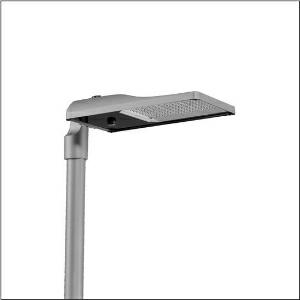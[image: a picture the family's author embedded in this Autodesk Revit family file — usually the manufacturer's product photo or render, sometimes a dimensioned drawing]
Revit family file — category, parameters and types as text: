
# Revit family: streetlight_sl_31_maxi___st0_5a_5xh8b31t08sa_315f
name_source: partatom
category: Lighting Fixtures
units: mm (PartAtom-declared; Revit-internal decimal feet)

## family parameters
Cut with Voids When Loaded = No
Host = Face
Light Source = No
Part Type = Normal
Room Calculation Point = No
Round Connector Dimension = Use Diameter
Shared = No

## types (1)
- --- (1 x LED, 28310 lm, 211.4 W, 3000K)
    Apparent Load = 211 VA
    CIE Flux Codes = 41 75 97 100 100
    Color Rendering = 70
    Color Temperature = 3000K
    Default Elevation = 1800 mm
    Description = Streetlight SL 31 maxi D4i, Desk-Remote mast luminaire for post-top, side-entry; light control with lens of PMMA; light distribution: ST0.5a, direct asymmetric distribution, for standard-compliant lighting for roads and squares; LED: luminous flux: 28.310lm, light colour: 730, colour temperature: 3000K; luminous efficacy: 133,9lm/W; control: pre-setting: logarithmic dimming characteristic, flexible luminous flux parameterisation, time-dependent luminous flux control, constant luminous flux control, power reduction, intelligent temperature release in ECG and LED module, overheat protection; luminaire housing, of diecast aluminium, SITECO metallic grey (DB 702S), corrosivity category C5 high according to DIN EN ISO 12944; cover of toughened safety glass, transparent, opened without tools; mast flange of diecast aluminium, SITECO metallic grey (DB 702S), spigot size: 76/60mm, mast flange included unmounted; cable length: 14,5m, connection cable pre-assembled; mains connection: 220..240V, AC, 50/60Hz; power consumption (at start of service life): 211,4W / (at end of service life): 238W / (with reduced operation 50%): 88,1W; protection rating (complete): IP66; insulation class (complete): insulation class II (safety insulation); impact resistance: IK09; certification: CE, ENEC, ENEC+, VDE, UKCA, ZD4i; permissible operating ambient temperature for outdoor applications: -40..+50°C; packaging unit: 1 piece

Light Distribution: ST0.5a
    Height = 79 mm
    Lamp = 1 x LED
    Lamp Light Flux = 28310 lm
    Lamp Power = 211.4 W
    Lamp count = 1
    Length = 657 mm
    Luminous efficacy = 134 lm/W
    Manufacturer = Siteco
    ModVariant = No
    Model = 5XH8B31T08SA
    Number of Poles = 1
    OnlyDefault = Yes
    Power Factor = 1
    Product Name = Streetlight SL 31 maxi | ST0.5a
    Product group = mast luminaire | pylon top
    ProductGroupID = 6100
    Protection Class = Protection class II
    Protection Degree = IP 66
    RLX_Detail_Level = 1
    RLX_Emergency_Light_Flux = 0 lm
    RLX_Emergency_Type = 0
    RLX_Emergency_Type_DB = No
    RlxData = <blob elided: 58161 chars, md5=983f4d62>
    Socket = socket
    Standby Power = 0 W
    System Light Flux = 28311 lm
    System Power = 211 W
    Type Comments = factory setting: luminous flux: 100 % | dim-lin: 254 | 727 mA
    Type Image = l_1300303.jpg
    URL = http://relux.com
    VarID = @adj_047017
    Voltage = 0 V
    Weight = 0.00 kg
    Width = 362 mm

## geometry (parser evidence)
native form markers: Blend x4, Sweep x11
no freeform markers — native parametric forms only
